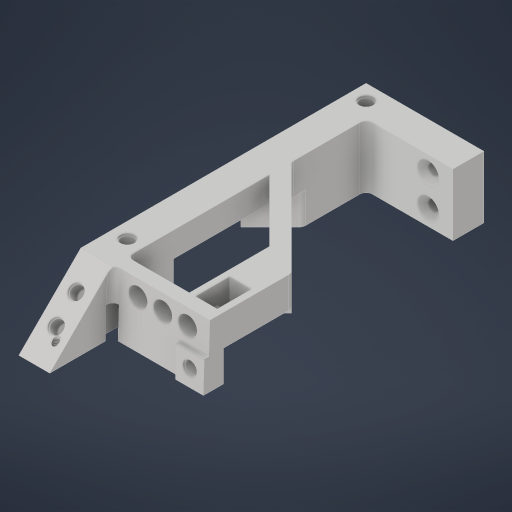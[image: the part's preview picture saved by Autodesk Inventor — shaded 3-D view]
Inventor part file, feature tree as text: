
AUTODESK INVENTOR PART (.ipt)
format: ipt  version: 2023 (Build 270158000, 158)  size: 546,304 bytes
history: native  units: in
note: dims shown in document units (in); Inventor stores cm internally (conversion verified against a paired STEP export)
features: sketch x24, extrude x17, hole x8, chamfer x1, plane x1, fillet x1
ambient origin geometry x8: Origin, YZ Plane, XZ Plane, XY Plane, X Axis, Y Axis, Z Axis, Center Point
bodies: Solid1 (feature_tree)
feature tree (52):
  extrude  "Extrusion1"  Depth=1.1024in TaperAngle=0.0deg
  extrude  "Extrusion4"  Depth=0.1181in
  hole  "Hole2"  [1 undecoded]
  hole  "Hole3"  [1 undecoded]
  hole  "Hole4"  [1 undecoded]
  hole  "Hole5"  [1 undecoded]
  sketch  "Sketch6"  dims[d19=4.4488in d22=0.1181in]
  hole  "Hole6"  [1 undecoded]
  extrude  "Extrusion5"  Depth=0.1969in
  sketch  "Sketch16"  dims[d51=0.1969in]
  hole  "Hole11"  [1 undecoded]
  extrude  "Extrusion22"  Depth=0.1969in
  extrude  "Extrusion23"  Depth=0.1969in
  chamfer  "Chamfer3"  Distance=1.378in
  extrude  "Extrusion24"  Depth=0.1181in
  extrude  "Extrusion25"  Depth=0.1969in
  extrude  "Extrusion26"  Depth=1.3386in TaperAngle=0.0deg
  extrude  "Extrusion28"  Depth=1.3386in
  extrude  "Extrusion29"  Depth=0.7874in
  extrude  "Extrusion30"  Depth=0.315in TaperAngle=0.0deg
  extrude  "Extrusion31"  Depth=0.7874in
  plane  "Work Plane4"
  extrude  "Extrusion32"  TaperAngle=45.0deg  [1 undecoded]
  extrude  "Extrusion33"  Depth=0.0787in
  extrude  "Extrusion34"  Depth=1.0236in
  extrude  "Extrusion35"  Depth=0.2756in
  extrude  "Extrusion36"  Depth=0.315in
  hole  "Hole13"  [1 undecoded]
  hole  "Hole12"  [1 undecoded]
  fillet  "Fillet1"  Radius=1.3386in
  sketch  "Sketch4"  dims[d4=0.3937in d5=0.0in d15=1.1024in d16=0.0in]
  sketch  "Sketch7"  dims[d23=0.1181in d25=0.0787in]
  sketch  "Sketch8"  dims[d26=0.7874in d27=0.3937in]
  sketch  "Sketch9"  dims[d39=0.1181in d40=0.1969in]
  sketch  "Sketch10"  dims[d41=0.079in d42=0.197in d43=0.1575in d44=0.0394in d45=0.5635in d46=0.299in d47=0.0in d48=0.1969in]
  sketch  "Sketch12"  dims[d49=1.1811in d50=0.1969in]
  sketch  "Sketch35"  dims[d54=0.2362in d55=0.3937in d56=0.2559in d57=0.0787in d58=0.5635in d59=0.2362in d60=0.0in d61=0.1969in]
  sketch  "Sketch36"  dims[d62=0.1969in d63=0.3937in]
  sketch  "Sketch37"  dims[d64=0.3937in d65=0.1969in]
  sketch  "Sketch38"  dims[d66=0.1575in d67=0.3937in d68=0.1772in d69=0.0236in d70=0.5635in d71=0.1575in d72=0.0in d73=0.1969in]
  sketch  "Sketch39"  dims[d74=0.3937in]
  sketch  "Sketch41"  dims[d75=0.1969in]
  sketch  "Sketch42"  dims[d76=0.1969in]
  sketch  "Sketch43"  dims[d77=0.1575in d78=0.3937in d79=0.1772in d80=0.0236in d81=0.5635in d82=0.1575in d83=0.0in]
  sketch  "Sketch44"  dims[d84=0.315in]
  sketch  "Sketch45"  dims[d85=0.1969in]
  sketch  "Sketch46"  dims[d86=0.315in]
  sketch  "Sketch47"  dims[d87=0.1969in]
  sketch  "Sketch48"  dims[d88=0.1339in d89=0.3937in d90=0.2717in d91=0.25in d92=0.6181in d93=0.3937in d94=0.8108in]
  sketch  "Sketch49"  dims[d97=0.5118in]
  sketch  "Sketch50"  dims[d98=0.1969in d106=1.378in d107=0.0in]
  sketch  "Sketch51"  dims[d124=0.1181in d125=0.1181in d240=0.1575in d241=0.2362in d242=0.1772in d243=0.0236in d244=90.0deg d245=0.1575in d246=0.0in d247=0.1969in d248=1.3386in d249=0.0in d250=1.3386in d251=0.7874in d252=0.1378in d253=0.0in d254=0.7874in d255=0.0787in d256=0.0118in d258=45.0deg d259=0.0787in d260=1.0236in d261=0.2756in d262=0.1378in d263=0.1181in d264=0.4724in d265=0.0in d266=1.3386in d267=0.1969in d268=0.7874in d269=0.0in d270=0.1181in d271=0.3937in d272=0.3937in d273=0.7874in d274=0.0in d279=0.1772in d280=0.2067in d281=0.1575in d282=0.2362in d283=0.1772in d284=0.0236in d285=90.0deg d286=0.1575in d287=0.0in d288=0.1772in d289=0.2067in d290=0.1339in d291=0.2362in d292=0.2717in d293=0.0236in d294=0.6181in d295=0.1575in d296=0.0in d297=0.5118in d298=0.4331in d299=0.3937in d300=0.0in d301=0.0787in d302=0.2756in d303=0.4331in d304=0.3937in d305=0.0in d306=0.1575in d307=0.1181in d308=0.1575in d309=0.3937in d310=0.0in d311=0.1969in d312=0.3937in d313=0.315in d314=0.315in d315=0.315in d316=0.2362in d317=0.2362in d318=0.2362in d319=0.2362in d320=0.3937in d321=0.0in d322=0.1969in d323=0.315in d324=0.315in d325=0.315in d326=0.2362in d327=0.2362in d328=0.2362in d329=0.3937in d330=0.0in d331=0.2756in d332=0.3937in d333=0.1575in d334=0.0in d335=0.0787in d336=0.3937in d337=0.0in d338=0.3937in d339=0.3543in d340=0.0591in d341=0.0in d342=0.3543in d343=0.3937in d344=0.0591in d345=0.0in d346=0.0787in d95=0.3937in d96=0.8108in d99=0.315in]
note: 9 required parameter values undecoded (feature->parameter linkage not recoverable at this tier; creation-order binding heuristic only, values carry confidence <= 0.55)
